# Revit family: CENTUM Halter XL120
name_source: partatom
category: HLS-Bauteile
revit_build: Autodesk Revit 2017 (Build: 20190507_1515(x64)
units: mm (PartAtom-declared; Revit-internal decimal feet)

## family parameters
Basisbauteil = Fläche
Beim Laden mit Abzugskörper schneiden = Nein
Bemaßung runder Anschluss = Durchmesser verwenden
Gemeinsam genutzt = Ja
Raumberechnungspunkt = Nein
Teiletyp = Normal

## types (1)
- CENTUM Halter XL120
    Artikelnummer = 1621201000
    Ausrichtung Platte = längs
    Befestigung = Baukörper
    Breite Platte = 220 mm  [stored 0.721785 ft]
    EAN = 4250928436740
    Fabrikat = MEFA
    Firma = MEFA Befestigungs- und Montagesysteme GmbH
    Gewicht = 6.71 kg
    Gewicht pro Bauteil = 6.71 kg
    Kurztext1 = Halter CENTUM längs
    Kurztext2 = für CENTUM XL 120 fsv
    Langloch = 27x18 mm
    Lochabstand = 150/170 mm
    Länge = 0 mm  [stored 0 ft]
    Länge Platte = 240 mm  [stored 0.787402 ft]
    Material = Stahl
    Oberflaeche = feuerstückverzinkt
    Profil = CENTUM
    Profilname = XL 120
    Profiltyp = XL 120
    Sicherheitsfaktor = 1.54
    Stärke Platte = 12 mm  [stored 0.0393701 ft]
    Vorgabe-Ansicht = 1219 mm
    max. Profilhöhe = 120 mm  [stored 0.393701 ft]
    max. zul. Last Druck = 0.00 kip

note: [stored X ft] marks values corroborated as IEEE doubles in the binary element streams (Revit-internal decimal feet)
